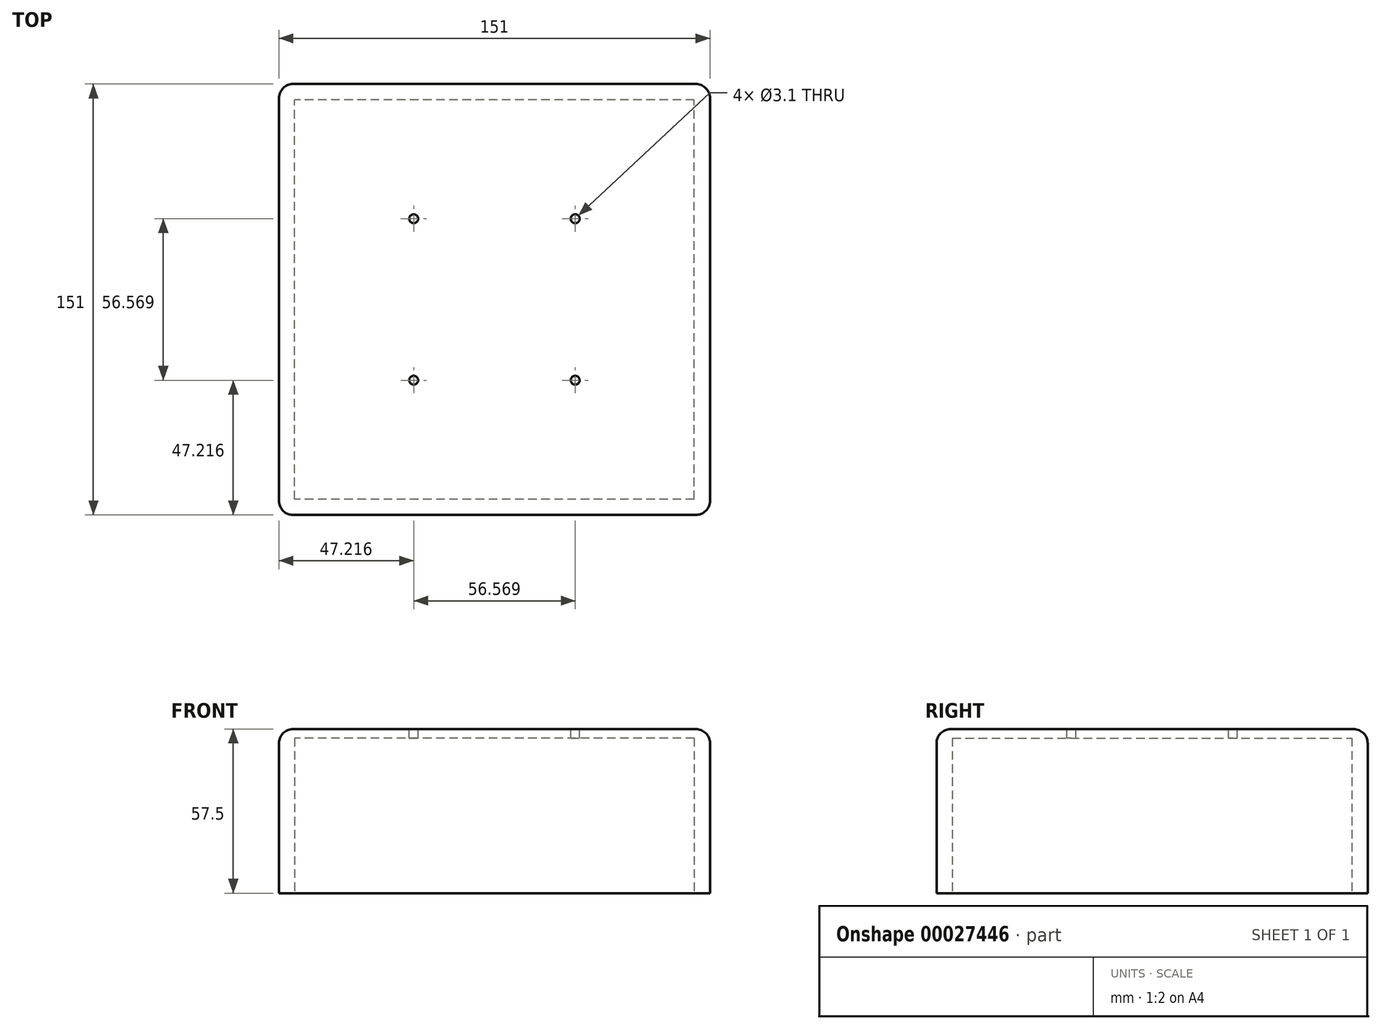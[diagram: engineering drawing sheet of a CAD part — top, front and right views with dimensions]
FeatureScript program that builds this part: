
annotation { "Feature Type Name" : "Feature", "Feature Type Description" : "" }
export const myFeature = defineFeature(function(context is Context, id is Id, definition is map)
    precondition{}
    {
        {
            var Q0;
            Q0=qCreatedBy(makeId("Top.planeOp"),FACE);
            var sketch = newSketch(context, id + "F0", { "sketchPlane" : qUnion([Q0])});
            skLineSegment(sketch, "E0.rect.bottom", {"start": v(-75.5, 75.5) * mm, "end": v(75.5, 75.5) * mm});
            skLineSegment(sketch, "E0.rect.top", {"start": v(-75.5, -75.5) * mm, "end": v(75.5, -75.5) * mm});
            skLineSegment(sketch, "E0.rect.left", {"start": v(-75.5, 75.5) * mm, "end": v(-75.5, -75.5) * mm});
            skLineSegment(sketch, "E0.rect.right", {"start": v(75.5, 75.5) * mm, "end": v(75.5, -75.5) * mm});
            skPoint(sketch, "E0.rect.middle", {"position": v(0, 0) * mm});
            skSolve(sketch);
        }
        {
            var Q0;
            Q0 = qSketchRegion(id + "F0", true);
            extrude(context, id + "F1", {"entities" : qUnion([Q0]), "depth" : 57.5 * mm});
        }
        {
            var Q0;
            Q0=makeQuery(id+"F1.opExtrude","CAP_FACE",FACE,{"disambiguationData":[OSD([sQuery(id+"F0.wireOp",EDGE,"E0.rect.bottom"),sQuery(id+"F0.wireOp",EDGE,"E0.rect.top"),sQuery(id+"F0.wireOp",EDGE,"E0.rect.left"),sQuery(id+"F0.wireOp",EDGE,"E0.rect.right")])],"isStart":true});
            var sketch = newSketch(context, id + "F2", { "sketchPlane" : qUnion([Q0])});
            skLineSegment(sketch, "E1.rect.bottom", {"start": v(70, 70) * mm, "end": v(-70, 70) * mm});
            skLineSegment(sketch, "E1.rect.top", {"start": v(70, -70) * mm, "end": v(-70, -70) * mm});
            skLineSegment(sketch, "E1.rect.left", {"start": v(70, 70) * mm, "end": v(70, -70) * mm});
            skLineSegment(sketch, "E1.rect.right", {"start": v(-70, 70) * mm, "end": v(-70, -70) * mm});
            skPoint(sketch, "E1.rect.middle", {"position": v(0, 0) * mm});
            skSolve(sketch);
        }
        {
            var Q0;
            Q0 = qSketchRegion(id + "F2", true);
            extrude(context, id + "F3", {"entities" : qUnion([Q0]), "operationType" : NewBodyOperationType.REMOVE, "oppositeDirection" : true, "depth" : 54.35 * mm});
        }
        {
            var Q0;
            Q0=makeQuery(id+"F1.opExtrude","CAP_EDGE",EDGE,{"disambiguationData":[OSD([sQuery(id+"F0.wireOp",EDGE,"E0.rect.top")])],"isStart":false});
            var Q1;
            Q1=makeQuery(id+"F1.opExtrude","CAP_EDGE",EDGE,{"disambiguationData":[OSD([sQuery(id+"F0.wireOp",EDGE,"E0.rect.left")])],"isStart":false});
            var Q2;
            Q2=makeQuery(id+"F1.opExtrude","CAP_EDGE",EDGE,{"disambiguationData":[OSD([sQuery(id+"F0.wireOp",EDGE,"E0.rect.bottom")])],"isStart":false});
            var Q3;
            Q3=makeQuery(id+"F1.opExtrude","CAP_EDGE",EDGE,{"disambiguationData":[OSD([sQuery(id+"F0.wireOp",EDGE,"E0.rect.right")])],"isStart":false});
            var Q4;
            Q4=makeQuery(id+"F1.opExtrude","SWEPT_EDGE",EDGE,{"disambiguationData":[OSD([sQuery(id+"F0.wireOp",EDGE,"E0.rect.top"),sQuery(id+"F0.wireOp",EDGE,"E0.rect.right")])]});
            var Q5;
            Q5=makeQuery(id+"F1.opExtrude","SWEPT_EDGE",EDGE,{"disambiguationData":[OSD([sQuery(id+"F0.wireOp",EDGE,"E0.rect.bottom"),sQuery(id+"F0.wireOp",EDGE,"E0.rect.right")])]});
            var Q6;
            Q6=makeQuery(id+"F1.opExtrude","SWEPT_EDGE",EDGE,{"disambiguationData":[OSD([sQuery(id+"F0.wireOp",EDGE,"E0.rect.top"),sQuery(id+"F0.wireOp",EDGE,"E0.rect.left")])]});
            var Q7;
            Q7=makeQuery(id+"F1.opExtrude","SWEPT_EDGE",EDGE,{"disambiguationData":[OSD([sQuery(id+"F0.wireOp",EDGE,"E0.rect.bottom"),sQuery(id+"F0.wireOp",EDGE,"E0.rect.left")])]});
            fillet(context, id + "F4", {"entities" : qUnion([Q0, Q1, Q2, Q3, Q4, Q5, Q6, Q7]), "radius" : 5 * mm, "tangentPropagation" : true, "allowEdgeOverflow" : false});
        }
        {
            var Q0;
            Q0=makeQuery(id+"F1.opExtrude","CAP_FACE",FACE,{"disambiguationData":[OSD([sQuery(id+"F0.wireOp",EDGE,"E0.rect.bottom"),sQuery(id+"F0.wireOp",EDGE,"E0.rect.top"),sQuery(id+"F0.wireOp",EDGE,"E0.rect.left"),sQuery(id+"F0.wireOp",EDGE,"E0.rect.right")])],"isStart":false});
            var sketch = newSketch(context, id + "F5", { "sketchPlane" : qUnion([Q0])});
            skLineSegment(sketch, "E2", {"start": v(-63.69, 50.6) * mm, "end": v(-43.68, 58.1) * mm});
            skLineSegment(sketch, "E3", {"start": v(-43.68, 58.1) * mm, "end": v(-47.91, 22.9) * mm});
            skLineSegment(sketch, "E4", {"start": v(-47.91, 22.9) * mm, "end": v(-25.4, 32.33) * mm});
            skLineSegment(sketch, "E5", {"start": v(-25.4, 32.33) * mm, "end": v(-27.9, 20.01) * mm});
            skLineSegment(sketch, "E6", {"start": v(-27.9, 20.01) * mm, "end": v(-57.92, 9.62) * mm});
            skLineSegment(sketch, "E7", {"start": v(-57.92, 9.62) * mm, "end": v(-50.03, 48.1) * mm});
            skLineSegment(sketch, "E8", {"start": v(-50.03, 48.1) * mm, "end": v(-62.15, 44.83) * mm});
            skLineSegment(sketch, "E9", {"start": v(-62.15, 44.83) * mm, "end": v(-63.69, 50.6) * mm});
            skLineSegment(sketch, "E10", {"start": v(-38.48, 57.92) * mm, "end": v(-38.48, 51.37) * mm});
            skLineSegment(sketch, "E11", {"start": v(-38.48, 51.37) * mm, "end": v(-30.02, 51.37) * mm});
            skLineSegment(sketch, "E12", {"start": v(-30.02, 51.37) * mm, "end": v(-30.02, 39.25) * mm});
            skLineSegment(sketch, "E13", {"start": v(-30.02, 39.25) * mm, "end": v(-38.48, 39.25) * mm});
            skLineSegment(sketch, "E14", {"start": v(-38.48, 39.25) * mm, "end": v(-38.48, 33.87) * mm});
            skLineSegment(sketch, "E15", {"start": v(-38.48, 33.87) * mm, "end": v(-17.7, 33.87) * mm});
            skLineSegment(sketch, "E16", {"start": v(-17.7, 33.87) * mm, "end": v(-17.7, 38.87) * mm});
            skLineSegment(sketch, "E17", {"start": v(-17.7, 38.87) * mm, "end": v(-24.63, 38.87) * mm});
            skLineSegment(sketch, "E18", {"start": v(-24.63, 38.87) * mm, "end": v(-24.63, 50.99) * mm});
            skLineSegment(sketch, "E19", {"start": v(-24.63, 50.99) * mm, "end": v(-17.12, 50.99) * mm});
            skLineSegment(sketch, "E20", {"start": v(-17.12, 50.99) * mm, "end": v(-17.12, 56.57) * mm});
            skLineSegment(sketch, "E21", {"start": v(-17.12, 56.57) * mm, "end": v(-38.48, 57.92) * mm});
            skLineSegment(sketch, "E22", {"start": v(-13.08, 56.57) * mm, "end": v(-17.12, 19.82) * mm});
            skLineSegment(sketch, "E23", {"start": v(-17.12, 19.82) * mm, "end": v(-10.96, 19.14) * mm});
            skLineSegment(sketch, "E24", {"start": v(-10.96, 19.14) * mm, "end": v(-8.8, 38.7) * mm});
            skLineSegment(sketch, "E25", {"start": v(-8.8, 38.7) * mm, "end": v(1.6, 37.55) * mm});
            skLineSegment(sketch, "E26", {"start": v(1.6, 37.55) * mm, "end": v(7.7, 41.37) * mm});
            skLineSegment(sketch, "E27", {"start": v(7.7, 41.37) * mm, "end": v(8.27, 48.49) * mm});
            skLineSegment(sketch, "E28", {"start": v(8.27, 48.49) * mm, "end": v(6.16, 51.57) * mm});
            skLineSegment(sketch, "E29", {"start": v(6.16, 51.57) * mm, "end": v(1.92, 53.3) * mm});
            skLineSegment(sketch, "E30", {"start": v(1.92, 53.3) * mm, "end": v(-13.08, 56.57) * mm});
            skLineSegment(sketch, "E31", {"start": v(-7.5, 48.1) * mm, "end": v(-7.5, 43.49) * mm});
            skLineSegment(sketch, "E32", {"start": v(-7.5, 43.49) * mm, "end": v(0, 43.3) * mm});
            skLineSegment(sketch, "E33", {"start": v(0, 43.3) * mm, "end": v(2.3, 45.22) * mm});
            skLineSegment(sketch, "E34", {"start": v(2.3, 45.22) * mm, "end": v(0, 47.99) * mm});
            skLineSegment(sketch, "E35", {"start": v(0, 47.99) * mm, "end": v(-7.5, 48.1) * mm});
            skLineSegment(sketch, "E36", {"start": v(-4.62, 33.87) * mm, "end": v(-8.85, -3.27) * mm});
            skLineSegment(sketch, "E37", {"start": v(-8.85, -3.27) * mm, "end": v(15.49, -6.05) * mm});
            skLineSegment(sketch, "E38", {"start": v(15.49, -6.05) * mm, "end": v(15.49, 3.85) * mm});
            skLineSegment(sketch, "E39", {"start": v(15.49, 3.85) * mm, "end": v(-0.77, 5.39) * mm});
            skLineSegment(sketch, "E40", {"start": v(-0.77, 5.39) * mm, "end": v(1.84, 32.97) * mm});
            skLineSegment(sketch, "E41", {"start": v(1.84, 32.97) * mm, "end": v(-4.62, 33.87) * mm});
            skLineSegment(sketch, "E42", {"start": v(10.97, 51.95) * mm, "end": v(10.97, 15.59) * mm});
            skLineSegment(sketch, "E43", {"start": v(10.97, 15.59) * mm, "end": v(16.55, 8.85) * mm});
            skLineSegment(sketch, "E44", {"start": v(16.55, 8.85) * mm, "end": v(31.36, 8.85) * mm});
            skLineSegment(sketch, "E45", {"start": v(31.36, 8.85) * mm, "end": v(38.3, 15.59) * mm});
            skLineSegment(sketch, "E46", {"start": v(38.3, 15.59) * mm, "end": v(38.3, 52.53) * mm});
            skLineSegment(sketch, "E47", {"start": v(38.3, 52.53) * mm, "end": v(32.9, 58.3) * mm});
            skLineSegment(sketch, "E48", {"start": v(32.9, 58.3) * mm, "end": v(17.32, 58.3) * mm});
            skLineSegment(sketch, "E49", {"start": v(17.32, 58.3) * mm, "end": v(10.97, 51.95) * mm});
            skLineSegment(sketch, "E50", {"start": v(17.7, 49.07) * mm, "end": v(19.24, 51.37) * mm});
            skLineSegment(sketch, "E51", {"start": v(19.24, 51.37) * mm, "end": v(30.79, 51.37) * mm});
            skLineSegment(sketch, "E52", {"start": v(30.79, 51.37) * mm, "end": v(33.29, 48.3) * mm});
            skLineSegment(sketch, "E53", {"start": v(33.29, 48.3) * mm, "end": v(33.29, 16.36) * mm});
            skLineSegment(sketch, "E54", {"start": v(33.29, 16.36) * mm, "end": v(31.17, 13.85) * mm});
            skLineSegment(sketch, "E55", {"start": v(31.17, 13.85) * mm, "end": v(18.28, 13.85) * mm});
            skLineSegment(sketch, "E56", {"start": v(18.28, 13.85) * mm, "end": v(16.16, 16.93) * mm});
            skLineSegment(sketch, "E57", {"start": v(16.16, 16.93) * mm, "end": v(17.7, 49.07) * mm});
            skLineSegment(sketch, "E58", {"start": v(63.88, 45.6) * mm, "end": v(67.73, 49.84) * mm});
            skLineSegment(sketch, "E59", {"start": v(67.73, 49.84) * mm, "end": v(61.96, 55.22) * mm});
            skLineSegment(sketch, "E60", {"start": v(61.96, 55.22) * mm, "end": v(49.07, 56.19) * mm});
            skLineSegment(sketch, "E61", {"start": v(49.07, 56.19) * mm, "end": v(44.06, 49.84) * mm});
            skLineSegment(sketch, "E62", {"start": v(44.06, 49.84) * mm, "end": v(44.06, 16.16) * mm});
            skLineSegment(sketch, "E63", {"start": v(44.06, 16.16) * mm, "end": v(47.72, 10.4) * mm});
            skLineSegment(sketch, "E64", {"start": v(47.72, 10.4) * mm, "end": v(58.69, 10.4) * mm});
            skLineSegment(sketch, "E65", {"start": v(58.69, 10.4) * mm, "end": v(65.23, 13.08) * mm});
            skLineSegment(sketch, "E66", {"start": v(65.23, 13.08) * mm, "end": v(66.96, 17.9) * mm});
            skLineSegment(sketch, "E67", {"start": v(66.96, 17.9) * mm, "end": v(63.3, 19.43) * mm});
            skLineSegment(sketch, "E68", {"start": v(63.3, 19.43) * mm, "end": v(62.15, 15) * mm});
            skLineSegment(sketch, "E69", {"start": v(62.15, 15) * mm, "end": v(55.8, 14.82) * mm});
            skLineSegment(sketch, "E70", {"start": v(55.8, 14.82) * mm, "end": v(50.8, 15.78) * mm});
            skLineSegment(sketch, "E71", {"start": v(50.8, 15.78) * mm, "end": v(50.8, 47.14) * mm});
            skLineSegment(sketch, "E72", {"start": v(50.8, 47.14) * mm, "end": v(55.03, 50.41) * mm});
            skLineSegment(sketch, "E73", {"start": v(55.03, 50.41) * mm, "end": v(60.61, 50.03) * mm});
            skLineSegment(sketch, "E74", {"start": v(60.61, 50.03) * mm, "end": v(63.88, 45.6) * mm});
            skLineSegment(sketch, "E75", {"start": v(-54.45, -10.78) * mm, "end": v(-54.45, -56.76) * mm});
            skLineSegment(sketch, "E76", {"start": v(-54.45, -56.76) * mm, "end": v(-37.14, -56.76) * mm});
            skLineSegment(sketch, "E77", {"start": v(-37.14, -56.76) * mm, "end": v(-26.17, -55.22) * mm});
            skLineSegment(sketch, "E78", {"start": v(-26.17, -55.22) * mm, "end": v(-23.09, -50.03) * mm});
            skLineSegment(sketch, "E79", {"start": v(-23.09, -50.03) * mm, "end": v(-24.44, -42.72) * mm});
            skLineSegment(sketch, "E80", {"start": v(-24.44, -42.72) * mm, "end": v(-26.55, -36.56) * mm});
            skLineSegment(sketch, "E81", {"start": v(-26.55, -36.56) * mm, "end": v(-39.64, -33.1) * mm});
            skLineSegment(sketch, "E82", {"start": v(-39.64, -33.1) * mm, "end": v(-44.06, -32.71) * mm});
            skLineSegment(sketch, "E83", {"start": v(-44.06, -32.71) * mm, "end": v(-47.53, -32.71) * mm});
            skLineSegment(sketch, "E84", {"start": v(-47.53, -32.71) * mm, "end": v(-47.53, -29.05) * mm});
            skLineSegment(sketch, "E85", {"start": v(-47.53, -29.05) * mm, "end": v(-34.44, -26.55) * mm});
            skLineSegment(sketch, "E86", {"start": v(-34.44, -26.55) * mm, "end": v(-27.7, -23.47) * mm});
            skLineSegment(sketch, "E87", {"start": v(-27.7, -23.47) * mm, "end": v(-24.63, -18.86) * mm});
            skLineSegment(sketch, "E88", {"start": v(-24.63, -18.86) * mm, "end": v(-25.2, -10.2) * mm});
            skLineSegment(sketch, "E89", {"start": v(-25.2, -10.2) * mm, "end": v(-25.78, -8.66) * mm});
            skLineSegment(sketch, "E90", {"start": v(-25.78, -8.66) * mm, "end": v(-26.75, -6.35) * mm});
            skLineSegment(sketch, "E91", {"start": v(-26.75, -6.35) * mm, "end": v(-48.87, -5.96) * mm});
            skLineSegment(sketch, "E92", {"start": v(-48.87, -5.96) * mm, "end": v(-50.8, -5.96) * mm});
            skLineSegment(sketch, "E93", {"start": v(-50.8, -5.96) * mm, "end": v(-52.53, -5.96) * mm});
            skLineSegment(sketch, "E94", {"start": v(-52.53, -5.96) * mm, "end": v(-54.65, -9.04) * mm});
            skLineSegment(sketch, "E95", {"start": v(-54.65, -9.04) * mm, "end": v(-54.45, -10.78) * mm});
            skLineSegment(sketch, "E96", {"start": v(-21.94, -23.28) * mm, "end": v(-17.32, -18.09) * mm});
            skLineSegment(sketch, "E97", {"start": v(-17.32, -18.09) * mm, "end": v(-3.46, -18.09) * mm});
            skLineSegment(sketch, "E98", {"start": v(-3.46, -18.09) * mm, "end": v(2.12, -24.44) * mm});
            skLineSegment(sketch, "E99", {"start": v(2.12, -24.44) * mm, "end": v(2.12, -54.07) * mm});
            skLineSegment(sketch, "E100", {"start": v(2.12, -54.07) * mm, "end": v(-1.54, -57.53) * mm});
            skLineSegment(sketch, "E101", {"start": v(-1.54, -57.53) * mm, "end": v(-13.85, -57.53) * mm});
            skLineSegment(sketch, "E102", {"start": v(-13.85, -57.53) * mm, "end": v(-20.2, -53.1) * mm});
            skLineSegment(sketch, "E103", {"start": v(-20.2, -53.1) * mm, "end": v(-21.94, -23.28) * mm});
            skLineSegment(sketch, "E104", {"start": v(-16.36, -24.82) * mm, "end": v(-14.24, -22.7) * mm});
            skLineSegment(sketch, "E105", {"start": v(-14.24, -22.7) * mm, "end": v(-5.77, -22.9) * mm});
            skLineSegment(sketch, "E106", {"start": v(-5.77, -22.9) * mm, "end": v(-2.7, -25.78) * mm});
            skLineSegment(sketch, "E107", {"start": v(-2.7, -25.78) * mm, "end": v(0, -52.53) * mm});
            skLineSegment(sketch, "E108", {"start": v(0, -52.53) * mm, "end": v(-4.81, -54.65) * mm});
            skLineSegment(sketch, "E109", {"start": v(-4.81, -54.65) * mm, "end": v(-12.7, -54.45) * mm});
            skLineSegment(sketch, "E110", {"start": v(-12.7, -54.45) * mm, "end": v(-15.97, -51.95) * mm});
            skLineSegment(sketch, "E111", {"start": v(-15.97, -51.95) * mm, "end": v(-16.36, -24.82) * mm});
            skLineSegment(sketch, "E112", {"start": v(5.96, -21.94) * mm, "end": v(12.31, -16.74) * mm});
            skLineSegment(sketch, "E113", {"start": v(12.31, -16.74) * mm, "end": v(20.4, -28.67) * mm});
            skLineSegment(sketch, "E114", {"start": v(20.4, -28.67) * mm, "end": v(29.82, -16.74) * mm});
            skLineSegment(sketch, "E115", {"start": v(29.82, -16.74) * mm, "end": v(34.44, -21.94) * mm});
            skLineSegment(sketch, "E116", {"start": v(34.44, -21.94) * mm, "end": v(23.28, -37.52) * mm});
            skLineSegment(sketch, "E117", {"start": v(23.28, -37.52) * mm, "end": v(33.29, -48.49) * mm});
            skLineSegment(sketch, "E118", {"start": v(33.29, -48.49) * mm, "end": v(28.29, -53.1) * mm});
            skLineSegment(sketch, "E119", {"start": v(28.29, -53.1) * mm, "end": v(18.66, -42.33) * mm});
            skLineSegment(sketch, "E120", {"start": v(18.66, -42.33) * mm, "end": v(10, -51.37) * mm});
            skLineSegment(sketch, "E121", {"start": v(10, -51.37) * mm, "end": v(6.35, -47.72) * mm});
            skLineSegment(sketch, "E122", {"start": v(6.35, -47.72) * mm, "end": v(15, -39.64) * mm});
            skLineSegment(sketch, "E123", {"start": v(15, -39.64) * mm, "end": v(5.96, -21.94) * mm});
            skLineSegment(sketch, "E124", {"start": v(43.49, -29.25) * mm, "end": v(53.13, -34.98) * mm});
            skLineSegment(sketch, "E125", {"start": v(53.13, -34.98) * mm, "end": v(64.24, -27.99) * mm});
            skLineSegment(sketch, "E126", {"start": v(64.24, -27.99) * mm, "end": v(54.6, -22.26) * mm});
            skLineSegment(sketch, "E127", {"start": v(54.6, -22.26) * mm, "end": v(43.49, -29.25) * mm});
            skLineSegment(sketch, "E128", {"start": v(43.49, -29.25) * mm, "end": v(43.49, -40.6) * mm});
            skLineSegment(sketch, "E129", {"start": v(43.49, -40.6) * mm, "end": v(53.13, -46.33) * mm});
            skLineSegment(sketch, "E130", {"start": v(53.13, -46.33) * mm, "end": v(64.24, -39.34) * mm});
            skLineSegment(sketch, "E131", {"start": v(64.24, -39.34) * mm, "end": v(64.24, -27.99) * mm});
            skLineSegment(sketch, "E132", {"start": v(53.13, -34.98) * mm, "end": v(53.13, -46.33) * mm});
            skLineSegment(sketch, "E133", {"start": v(-46.32, -11.4) * mm, "end": v(-46.32, -21.32) * mm});
            skLineSegment(sketch, "E134", {"start": v(-46.32, -21.32) * mm, "end": v(-34.63, -20.59) * mm});
            skLineSegment(sketch, "E135", {"start": v(-34.63, -20.59) * mm, "end": v(-31.17, -15.59) * mm});
            skLineSegment(sketch, "E136", {"start": v(-31.17, -15.59) * mm, "end": v(-32.9, -11.4) * mm});
            skLineSegment(sketch, "E137", {"start": v(-32.9, -11.4) * mm, "end": v(-46.32, -11.4) * mm});
            skLineSegment(sketch, "E138", {"start": v(-47.33, -39.83) * mm, "end": v(-47.33, -48.3) * mm});
            skLineSegment(sketch, "E139", {"start": v(-47.33, -48.3) * mm, "end": v(-32.33, -49.26) * mm});
            skLineSegment(sketch, "E140", {"start": v(-32.33, -49.26) * mm, "end": v(-29.63, -46.18) * mm});
            skLineSegment(sketch, "E141", {"start": v(-29.63, -46.18) * mm, "end": v(-30.13, -42.73) * mm});
            skLineSegment(sketch, "E142", {"start": v(-30.13, -42.73) * mm, "end": v(-33.59, -40.43) * mm});
            skLineSegment(sketch, "E143", {"start": v(-33.59, -40.43) * mm, "end": v(-47.33, -39.83) * mm});
            skSolve(sketch);
        }
        {
            var Q0;
            Q0=makeQuery(id+"F5.imprint","IMPRINT",FACE,{"disambiguationData":[TD([[makeQuery(id+"F5.imprint","IMPRINT",EDGE,{"derivedFrom":sQuery(id+"F5.wireOp",EDGE,"E2")}),-1.0]])]});
            var Q1;
            Q1=makeQuery(id+"F5.imprint","IMPRINT",FACE,{"disambiguationData":[TD([[makeQuery(id+"F5.imprint","IMPRINT",EDGE,{"derivedFrom":sQuery(id+"F5.wireOp",EDGE,"E10")}),1.0]])]});
            var Q2;
            Q2=makeQuery(id+"F5.imprint","IMPRINT",FACE,{"disambiguationData":[TD([[makeQuery(id+"F5.imprint","IMPRINT",EDGE,{"derivedFrom":sQuery(id+"F5.wireOp",EDGE,"E22")}),1.0]])]});
            var Q3;
            Q3=makeQuery(id+"F5.imprint","IMPRINT",FACE,{"disambiguationData":[TD([[makeQuery(id+"F5.imprint","IMPRINT",EDGE,{"derivedFrom":sQuery(id+"F5.wireOp",EDGE,"E36")}),1.0]])]});
            var Q4;
            Q4=makeQuery(id+"F5.imprint","IMPRINT",FACE,{"disambiguationData":[TD([[makeQuery(id+"F5.imprint","IMPRINT",EDGE,{"derivedFrom":sQuery(id+"F5.wireOp",EDGE,"E42")}),1.0]])]});
            var Q5;
            Q5=makeQuery(id+"F5.imprint","IMPRINT",FACE,{"disambiguationData":[TD([[makeQuery(id+"F5.imprint","IMPRINT",EDGE,{"derivedFrom":sQuery(id+"F5.wireOp",EDGE,"E58")}),1.0]])]});
            var Q6;
            Q6=makeQuery(id+"F5.imprint","IMPRINT",FACE,{"disambiguationData":[TD([[makeQuery(id+"F5.imprint","IMPRINT",EDGE,{"derivedFrom":sQuery(id+"F5.wireOp",EDGE,"E124")}),1.0]])]});
            var Q7;
            Q7=makeQuery(id+"F5.imprint","IMPRINT",FACE,{"disambiguationData":[TD([[makeQuery(id+"F5.imprint","IMPRINT",EDGE,{"derivedFrom":sQuery(id+"F5.wireOp",EDGE,"E124")}),-1.0]])]});
            var Q8;
            Q8=makeQuery(id+"F5.imprint","IMPRINT",FACE,{"disambiguationData":[TD([[makeQuery(id+"F5.imprint","IMPRINT",EDGE,{"derivedFrom":sQuery(id+"F5.wireOp",EDGE,"E125")}),-1.0]])]});
            var Q9;
            Q9=makeQuery(id+"F5.imprint","IMPRINT",FACE,{"disambiguationData":[TD([[makeQuery(id+"F5.imprint","IMPRINT",EDGE,{"derivedFrom":sQuery(id+"F5.wireOp",EDGE,"E112")}),-1.0]])]});
            var Q10;
            Q10=makeQuery(id+"F5.imprint","IMPRINT",FACE,{"disambiguationData":[TD([[makeQuery(id+"F5.imprint","IMPRINT",EDGE,{"derivedFrom":sQuery(id+"F5.wireOp",EDGE,"E96")}),-1.0]])]});
            var Q11;
            Q11=makeQuery(id+"F5.imprint","IMPRINT",FACE,{"disambiguationData":[TD([[makeQuery(id+"F5.imprint","IMPRINT",EDGE,{"derivedFrom":sQuery(id+"F5.wireOp",EDGE,"E75")}),1.0]])]});
            extrude(context, id + "F6", {"entities" : qUnion([Q0, Q1, Q2, Q3, Q4, Q5, Q6, Q7, Q8, Q9, Q10, Q11]), "oppositeDirection" : true, "depth" : 10 * mm, "symmetric" : true});
        }
        {
            var Q0;
            Q0=makeQuery(id+"F6.opExtrude","SWEPT_BODY",BODY,{"disambiguationData":[OSD([sQuery(id+"F5.wireOp",EDGE,"E2"),sQuery(id+"F5.wireOp",EDGE,"E3"),sQuery(id+"F5.wireOp",EDGE,"E4"),sQuery(id+"F5.wireOp",EDGE,"E5"),sQuery(id+"F5.wireOp",EDGE,"E6"),sQuery(id+"F5.wireOp",EDGE,"E7"),sQuery(id+"F5.wireOp",EDGE,"E8"),sQuery(id+"F5.wireOp",EDGE,"E9")])]});
            var Q1;
            Q1=makeQuery(id+"F6.opExtrude","SWEPT_BODY",BODY,{"disambiguationData":[OSD([sQuery(id+"F5.wireOp",EDGE,"E10"),sQuery(id+"F5.wireOp",EDGE,"E11"),sQuery(id+"F5.wireOp",EDGE,"E12"),sQuery(id+"F5.wireOp",EDGE,"E13"),sQuery(id+"F5.wireOp",EDGE,"E14"),sQuery(id+"F5.wireOp",EDGE,"E15"),sQuery(id+"F5.wireOp",EDGE,"E16"),sQuery(id+"F5.wireOp",EDGE,"E17"),sQuery(id+"F5.wireOp",EDGE,"E18"),sQuery(id+"F5.wireOp",EDGE,"E19"),sQuery(id+"F5.wireOp",EDGE,"E20"),sQuery(id+"F5.wireOp",EDGE,"E21")])]});
            var Q2;
            Q2=makeQuery(id+"F6.opExtrude","SWEPT_BODY",BODY,{"disambiguationData":[OSD([sQuery(id+"F5.wireOp",EDGE,"E22"),sQuery(id+"F5.wireOp",EDGE,"E23"),sQuery(id+"F5.wireOp",EDGE,"E24"),sQuery(id+"F5.wireOp",EDGE,"E25"),sQuery(id+"F5.wireOp",EDGE,"E26"),sQuery(id+"F5.wireOp",EDGE,"E27"),sQuery(id+"F5.wireOp",EDGE,"E28"),sQuery(id+"F5.wireOp",EDGE,"E29"),sQuery(id+"F5.wireOp",EDGE,"E30"),sQuery(id+"F5.wireOp",EDGE,"E31"),sQuery(id+"F5.wireOp",EDGE,"E32"),sQuery(id+"F5.wireOp",EDGE,"E33"),sQuery(id+"F5.wireOp",EDGE,"E34"),sQuery(id+"F5.wireOp",EDGE,"E35")])]});
            var Q3;
            Q3=makeQuery(id+"F6.opExtrude","SWEPT_BODY",BODY,{"disambiguationData":[OSD([sQuery(id+"F5.wireOp",EDGE,"E36"),sQuery(id+"F5.wireOp",EDGE,"E37"),sQuery(id+"F5.wireOp",EDGE,"E38"),sQuery(id+"F5.wireOp",EDGE,"E39"),sQuery(id+"F5.wireOp",EDGE,"E40"),sQuery(id+"F5.wireOp",EDGE,"E41")])]});
            var Q4;
            Q4=makeQuery(id+"F6.opExtrude","SWEPT_BODY",BODY,{"disambiguationData":[OSD([sQuery(id+"F5.wireOp",EDGE,"E42"),sQuery(id+"F5.wireOp",EDGE,"E43"),sQuery(id+"F5.wireOp",EDGE,"E44"),sQuery(id+"F5.wireOp",EDGE,"E45"),sQuery(id+"F5.wireOp",EDGE,"E46"),sQuery(id+"F5.wireOp",EDGE,"E47"),sQuery(id+"F5.wireOp",EDGE,"E48"),sQuery(id+"F5.wireOp",EDGE,"E49"),sQuery(id+"F5.wireOp",EDGE,"E50"),sQuery(id+"F5.wireOp",EDGE,"E51"),sQuery(id+"F5.wireOp",EDGE,"E52"),sQuery(id+"F5.wireOp",EDGE,"E53"),sQuery(id+"F5.wireOp",EDGE,"E54"),sQuery(id+"F5.wireOp",EDGE,"E55"),sQuery(id+"F5.wireOp",EDGE,"E56"),sQuery(id+"F5.wireOp",EDGE,"E57")])]});
            var Q5;
            Q5=makeQuery(id+"F6.opExtrude","SWEPT_BODY",BODY,{"disambiguationData":[OSD([sQuery(id+"F5.wireOp",EDGE,"E58"),sQuery(id+"F5.wireOp",EDGE,"E59"),sQuery(id+"F5.wireOp",EDGE,"E60"),sQuery(id+"F5.wireOp",EDGE,"E61"),sQuery(id+"F5.wireOp",EDGE,"E62"),sQuery(id+"F5.wireOp",EDGE,"E63"),sQuery(id+"F5.wireOp",EDGE,"E64"),sQuery(id+"F5.wireOp",EDGE,"E65"),sQuery(id+"F5.wireOp",EDGE,"E66"),sQuery(id+"F5.wireOp",EDGE,"E67"),sQuery(id+"F5.wireOp",EDGE,"E68"),sQuery(id+"F5.wireOp",EDGE,"E69"),sQuery(id+"F5.wireOp",EDGE,"E70"),sQuery(id+"F5.wireOp",EDGE,"E71"),sQuery(id+"F5.wireOp",EDGE,"E72"),sQuery(id+"F5.wireOp",EDGE,"E73"),sQuery(id+"F5.wireOp",EDGE,"E74")])]});
            var Q6;
            Q6=makeQuery(id+"F6.opExtrude","SWEPT_BODY",BODY,{"disambiguationData":[OSD([sQuery(id+"F5.wireOp",EDGE,"E75"),sQuery(id+"F5.wireOp",EDGE,"E76"),sQuery(id+"F5.wireOp",EDGE,"E77"),sQuery(id+"F5.wireOp",EDGE,"E78"),sQuery(id+"F5.wireOp",EDGE,"E79"),sQuery(id+"F5.wireOp",EDGE,"E80"),sQuery(id+"F5.wireOp",EDGE,"E81"),sQuery(id+"F5.wireOp",EDGE,"E82"),sQuery(id+"F5.wireOp",EDGE,"E83"),sQuery(id+"F5.wireOp",EDGE,"E84"),sQuery(id+"F5.wireOp",EDGE,"E85"),sQuery(id+"F5.wireOp",EDGE,"E86"),sQuery(id+"F5.wireOp",EDGE,"E87"),sQuery(id+"F5.wireOp",EDGE,"E88"),sQuery(id+"F5.wireOp",EDGE,"E89"),sQuery(id+"F5.wireOp",EDGE,"E90"),sQuery(id+"F5.wireOp",EDGE,"E91"),sQuery(id+"F5.wireOp",EDGE,"E92"),sQuery(id+"F5.wireOp",EDGE,"E93"),sQuery(id+"F5.wireOp",EDGE,"E94"),sQuery(id+"F5.wireOp",EDGE,"E95"),sQuery(id+"F5.wireOp",EDGE,"E133"),sQuery(id+"F5.wireOp",EDGE,"E134"),sQuery(id+"F5.wireOp",EDGE,"E135"),sQuery(id+"F5.wireOp",EDGE,"E136"),sQuery(id+"F5.wireOp",EDGE,"E137"),sQuery(id+"F5.wireOp",EDGE,"E138"),sQuery(id+"F5.wireOp",EDGE,"E139"),sQuery(id+"F5.wireOp",EDGE,"E140"),sQuery(id+"F5.wireOp",EDGE,"E141"),sQuery(id+"F5.wireOp",EDGE,"E142"),sQuery(id+"F5.wireOp",EDGE,"E143")])]});
            var Q7;
            Q7=makeQuery(id+"F6.opExtrude","SWEPT_BODY",BODY,{"disambiguationData":[OSD([sQuery(id+"F5.wireOp",EDGE,"E96"),sQuery(id+"F5.wireOp",EDGE,"E97"),sQuery(id+"F5.wireOp",EDGE,"E98"),sQuery(id+"F5.wireOp",EDGE,"E99"),sQuery(id+"F5.wireOp",EDGE,"E100"),sQuery(id+"F5.wireOp",EDGE,"E101"),sQuery(id+"F5.wireOp",EDGE,"E102"),sQuery(id+"F5.wireOp",EDGE,"E103"),sQuery(id+"F5.wireOp",EDGE,"E104"),sQuery(id+"F5.wireOp",EDGE,"E105"),sQuery(id+"F5.wireOp",EDGE,"E106"),sQuery(id+"F5.wireOp",EDGE,"E107"),sQuery(id+"F5.wireOp",EDGE,"E108"),sQuery(id+"F5.wireOp",EDGE,"E109"),sQuery(id+"F5.wireOp",EDGE,"E110"),sQuery(id+"F5.wireOp",EDGE,"E111")])]});
            var Q8;
            Q8=makeQuery(id+"F6.opExtrude","SWEPT_BODY",BODY,{"disambiguationData":[OSD([sQuery(id+"F5.wireOp",EDGE,"E112"),sQuery(id+"F5.wireOp",EDGE,"E113"),sQuery(id+"F5.wireOp",EDGE,"E114"),sQuery(id+"F5.wireOp",EDGE,"E115"),sQuery(id+"F5.wireOp",EDGE,"E116"),sQuery(id+"F5.wireOp",EDGE,"E117"),sQuery(id+"F5.wireOp",EDGE,"E118"),sQuery(id+"F5.wireOp",EDGE,"E119"),sQuery(id+"F5.wireOp",EDGE,"E120"),sQuery(id+"F5.wireOp",EDGE,"E121"),sQuery(id+"F5.wireOp",EDGE,"E122"),sQuery(id+"F5.wireOp",EDGE,"E123")])]});
            var Q9;
            Q9=makeQuery(id+"F6.opExtrude","SWEPT_BODY",BODY,{"disambiguationData":[OSD([sQuery(id+"F5.wireOp",EDGE,"E126"),sQuery(id+"F5.wireOp",EDGE,"E127"),sQuery(id+"F5.wireOp",EDGE,"E128"),sQuery(id+"F5.wireOp",EDGE,"E129"),sQuery(id+"F5.wireOp",EDGE,"E130"),sQuery(id+"F5.wireOp",EDGE,"E131")])]});
            deleteBodies(context, id + "F7", {"entities" : qUnion([Q0, Q1, Q2, Q3, Q4, Q5, Q6, Q7, Q8, Q9])});
        }
        {
            var Q0;
            Q0=makeQuery(id+"F1.opExtrude","CAP_FACE",FACE,{"disambiguationData":[OSD([sQuery(id+"F0.wireOp",EDGE,"E0.rect.bottom"),sQuery(id+"F0.wireOp",EDGE,"E0.rect.top"),sQuery(id+"F0.wireOp",EDGE,"E0.rect.left"),sQuery(id+"F0.wireOp",EDGE,"E0.rect.right")])],"isStart":false});
            var sketch = newSketch(context, id + "F8", { "sketchPlane" : qUnion([Q0])});
            skLineSegment(sketch, "E144", {"start": v(70.5, 70.5) * mm, "end": v(-70.5, -70.5) * mm, "construction": true});
            skPoint(sketch, "E145", {"position": v(0, 0) * mm});
            skLineSegment(sketch, "E146", {"start": v(-70.5, 70.5) * mm, "end": v(70.5, -70.5) * mm, "construction": true});
            skCircle(sketch, "E147", {"center": v(28.28, 28.28) * mm, "radius": 1.55 * mm});
            skCircle(sketch, "E148", {"center": v(-28.28, 28.28) * mm, "radius": 1.55 * mm});
            skCircle(sketch, "E149", {"center": v(-28.28, -28.28) * mm, "radius": 1.55 * mm});
            skCircle(sketch, "E150", {"center": v(28.28, -28.28) * mm, "radius": 1.55 * mm});
            skLineSegment(sketch, "E151.0", {"start": v(70.5, 70.5) * mm, "end": v(-70.5, 70.5) * mm});
            skLineSegment(sketch, "E151.1", {"start": v(70.5, -70.5) * mm, "end": v(70.5, 70.5) * mm});
            skLineSegment(sketch, "E151.2", {"start": v(-70.5, 70.5) * mm, "end": v(-70.5, -70.5) * mm});
            skLineSegment(sketch, "E151.3", {"start": v(-70.5, -70.5) * mm, "end": v(70.5, -70.5) * mm});
            skSolve(sketch);
        }
        {
            var Q0;
            Q0=makeQuery(id+"F8.imprint","IMPRINT",FACE,{"disambiguationData":[TD([[makeQuery(id+"F8.imprint","IMPRINT",EDGE,{"derivedFrom":sQuery(id+"F8.wireOp",EDGE,"E148")}),1.0]])]});
            var Q1;
            Q1=makeQuery(id+"F8.imprint","IMPRINT",FACE,{"disambiguationData":[TD([[makeQuery(id+"F8.imprint","IMPRINT",EDGE,{"derivedFrom":sQuery(id+"F8.wireOp",EDGE,"E149")}),1.0]])]});
            var Q2;
            Q2=makeQuery(id+"F8.imprint","IMPRINT",FACE,{"disambiguationData":[TD([[makeQuery(id+"F8.imprint","IMPRINT",EDGE,{"derivedFrom":sQuery(id+"F8.wireOp",EDGE,"E150")}),1.0]])]});
            var Q3;
            Q3=makeQuery(id+"F8.imprint","IMPRINT",FACE,{"disambiguationData":[TD([[makeQuery(id+"F8.imprint","IMPRINT",EDGE,{"derivedFrom":sQuery(id+"F8.wireOp",EDGE,"E147")}),1.0]])]});
            extrude(context, id + "F9", {"entities" : qUnion([Q0, Q1, Q2, Q3]), "operationType" : NewBodyOperationType.REMOVE, "endBound" : BoundingType.THROUGH_ALL, "oppositeDirection" : true, "depth" : 25 * mm});
        }
    });
